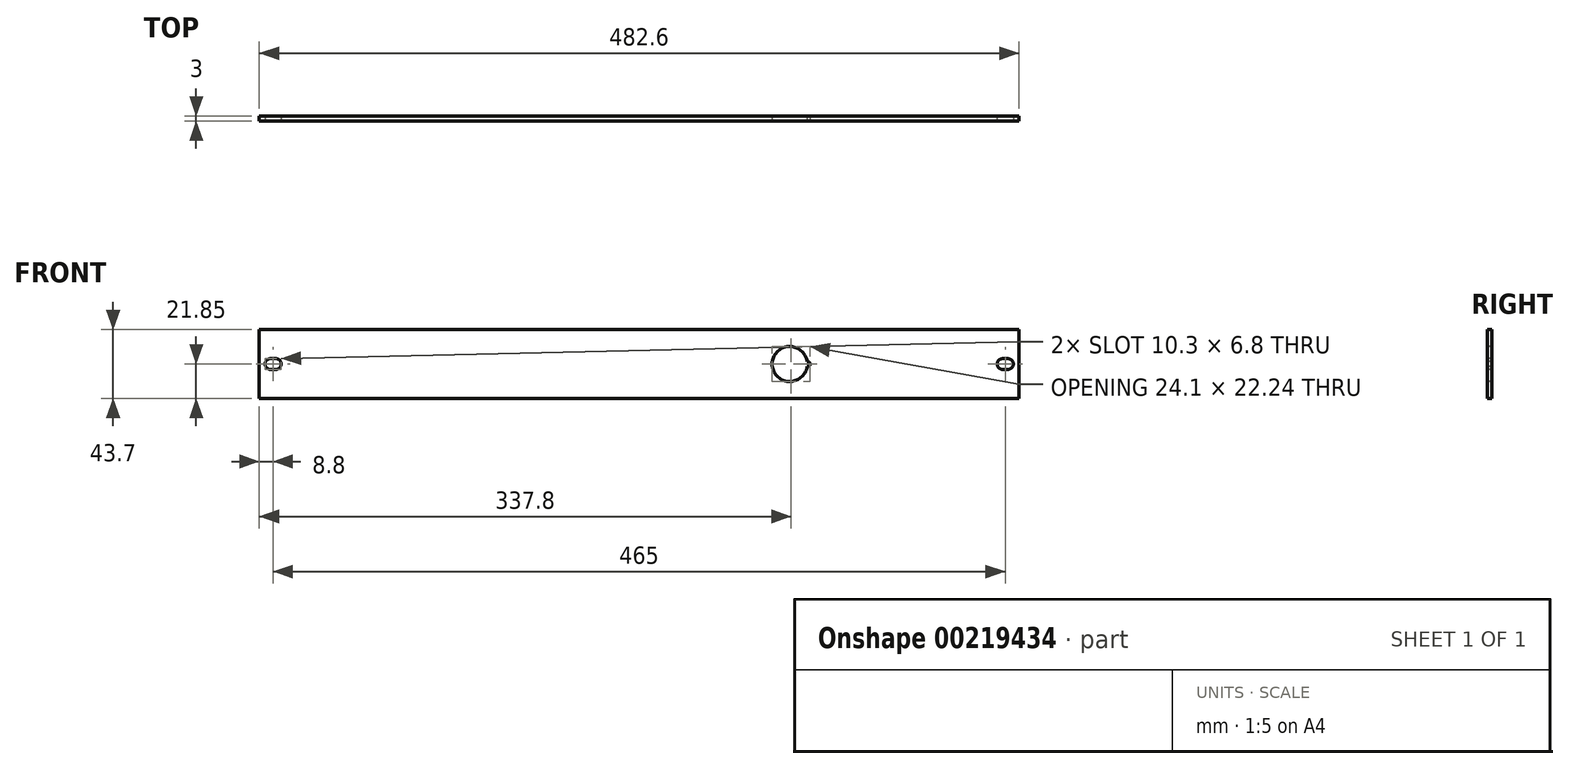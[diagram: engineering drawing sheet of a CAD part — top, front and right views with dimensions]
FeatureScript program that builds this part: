
annotation { "Feature Type Name" : "Feature", "Feature Type Description" : "" }
export const myFeature = defineFeature(function(context is Context, id is Id, definition is map)
    precondition{}
    {
        {
            var Q0;
            Q0=qCreatedBy(makeId("Front.planeOp"),FACE);
            var sketch = newSketch(context, id + "F0", { "sketchPlane" : qUnion([Q0])});
            skLineSegment(sketch, "E0.bottom", {"start": v(-241.3, -21.85) * mm, "end": v(241.3, -21.85) * mm});
            skLineSegment(sketch, "E0.top", {"start": v(-241.3, 21.85) * mm, "end": v(241.3, 21.85) * mm});
            skLineSegment(sketch, "E0.left", {"start": v(-241.3, -21.85) * mm, "end": v(-241.3, 21.85) * mm});
            skLineSegment(sketch, "E0.right", {"start": v(241.3, -21.85) * mm, "end": v(241.3, 21.85) * mm});
            skPoint(sketch, "E0.middle", {"position": v(0, 0) * mm});
            skSolve(sketch);
        }
        {
            var Q0;
            Q0=makeQuery(id+"F0.imprint","IMPRINT",FACE,{"disambiguationData":[TD([[makeQuery(id+"F0.imprint","IMPRINT",EDGE,{"derivedFrom":sQuery(id+"F0.wireOp",EDGE,"E0.bottom")}),1.0]])]});
            extrude(context, id + "F1", {"entities" : qUnion([Q0]), "oppositeDirection" : true, "depth" : 3 * mm});
        }
        {
            var Q0;
            Q0=makeQuery(id+"F1.opExtrude","CAP_FACE",FACE,{"disambiguationData":[OSD([sQuery(id+"F0.wireOp",EDGE,"E0.bottom"),sQuery(id+"F0.wireOp",EDGE,"E0.top"),sQuery(id+"F0.wireOp",EDGE,"E0.left"),sQuery(id+"F0.wireOp",EDGE,"E0.right")])],"isStart":true});
            var sketch = newSketch(context, id + "F2", { "sketchPlane" : qUnion([Q0])});
            skLineSegment(sketch, "E1.bottom", {"start": v(-230.75, -3.4) * mm, "end": v(-234.25, -3.4) * mm});
            skLineSegment(sketch, "E1.top", {"start": v(-230.75, 3.4) * mm, "end": v(-234.25, 3.4) * mm});
            skLineSegment(sketch, "E1.left", {"start": v(-230.75, -3.4) * mm, "end": v(-230.75, 3.4) * mm});
            skLineSegment(sketch, "E1.right", {"start": v(-234.25, -3.4) * mm, "end": v(-234.25, 3.4) * mm});
            skPoint(sketch, "E1.middle", {"position": v(-232.5, 0) * mm});
            skArc(sketch, "E2", {"start": v(-230.75, -3.4) * mm, "mid": v(-227.35, 0) * mm, "end": v(-230.75, 3.4) * mm});
            skArc(sketch, "E3", {"start": v(-234.25, 3.4) * mm, "mid": v(-237.65, 0) * mm, "end": v(-234.25, -3.4) * mm});
            skSolve(sketch);
        }
        {
            var Q0;
            Q0=makeQuery(id+"F2.imprint","IMPRINT",FACE,{"disambiguationData":[TD([[makeQuery(id+"F2.imprint","IMPRINT",EDGE,{"derivedFrom":sQuery(id+"F2.wireOp",EDGE,"E1.bottom")}),1.0]])]});
            var sketch = newSketch(context, id + "F3", { "sketchPlane" : qUnion([Q0])});
            skLineSegment(sketch, "E4.bottom", {"start": v(234.25, -3.4) * mm, "end": v(230.75, -3.4) * mm});
            skLineSegment(sketch, "E4.top", {"start": v(234.25, 3.4) * mm, "end": v(230.75, 3.4) * mm});
            skLineSegment(sketch, "E4.left", {"start": v(234.25, -3.4) * mm, "end": v(234.25, 3.4) * mm});
            skLineSegment(sketch, "E4.right", {"start": v(230.75, -3.4) * mm, "end": v(230.75, 3.4) * mm});
            skPoint(sketch, "E4.middle", {"position": v(232.5, 0) * mm});
            skArc(sketch, "E5", {"start": v(230.75, 3.4) * mm, "mid": v(227.35, 0) * mm, "end": v(230.75, -3.4) * mm});
            skArc(sketch, "E6", {"start": v(234.25, -3.4) * mm, "mid": v(237.65, 0) * mm, "end": v(234.25, 3.4) * mm});
            skSolve(sketch);
        }
        {
            var Q0;
            Q0=qSketchRegion(id+"F2",true);
            var Q1;
            Q1=qSketchRegion(id+"F3",true);
            extrude(context, id + "F4", {"entities" : qUnion([Q0, Q1]), "operationType" : NewBodyOperationType.REMOVE, "oppositeDirection" : true, "depth" : 3 * mm});
        }
        {
            var Q0;
            Q0=makeQuery(id+"F1.opExtrude","CAP_FACE",FACE,{"disambiguationData":[OSD([sQuery(id+"F0.wireOp",EDGE,"E0.bottom"),sQuery(id+"F0.wireOp",EDGE,"E0.top"),sQuery(id+"F0.wireOp",EDGE,"E0.left"),sQuery(id+"F0.wireOp",EDGE,"E0.right")])],"isStart":true});
            var sketch = newSketch(context, id + "F5", { "sketchPlane" : qUnion([Q0])});
            skCircle(sketch, "E7", {"center": v(106.95, 0) * mm, "radius": 1.6 * mm});
            skCircle(sketch, "E8", {"center": v(95.6, 0) * mm, "radius": 11.15 * mm});
            skSolve(sketch);
        }
        {
            var Q0;
            Q0=qSketchRegion(id+"F5",true);
            extrude(context, id + "F6", {"entities" : qUnion([Q0]), "operationType" : NewBodyOperationType.REMOVE, "oppositeDirection" : true, "depth" : 3 * mm});
        }
    });
